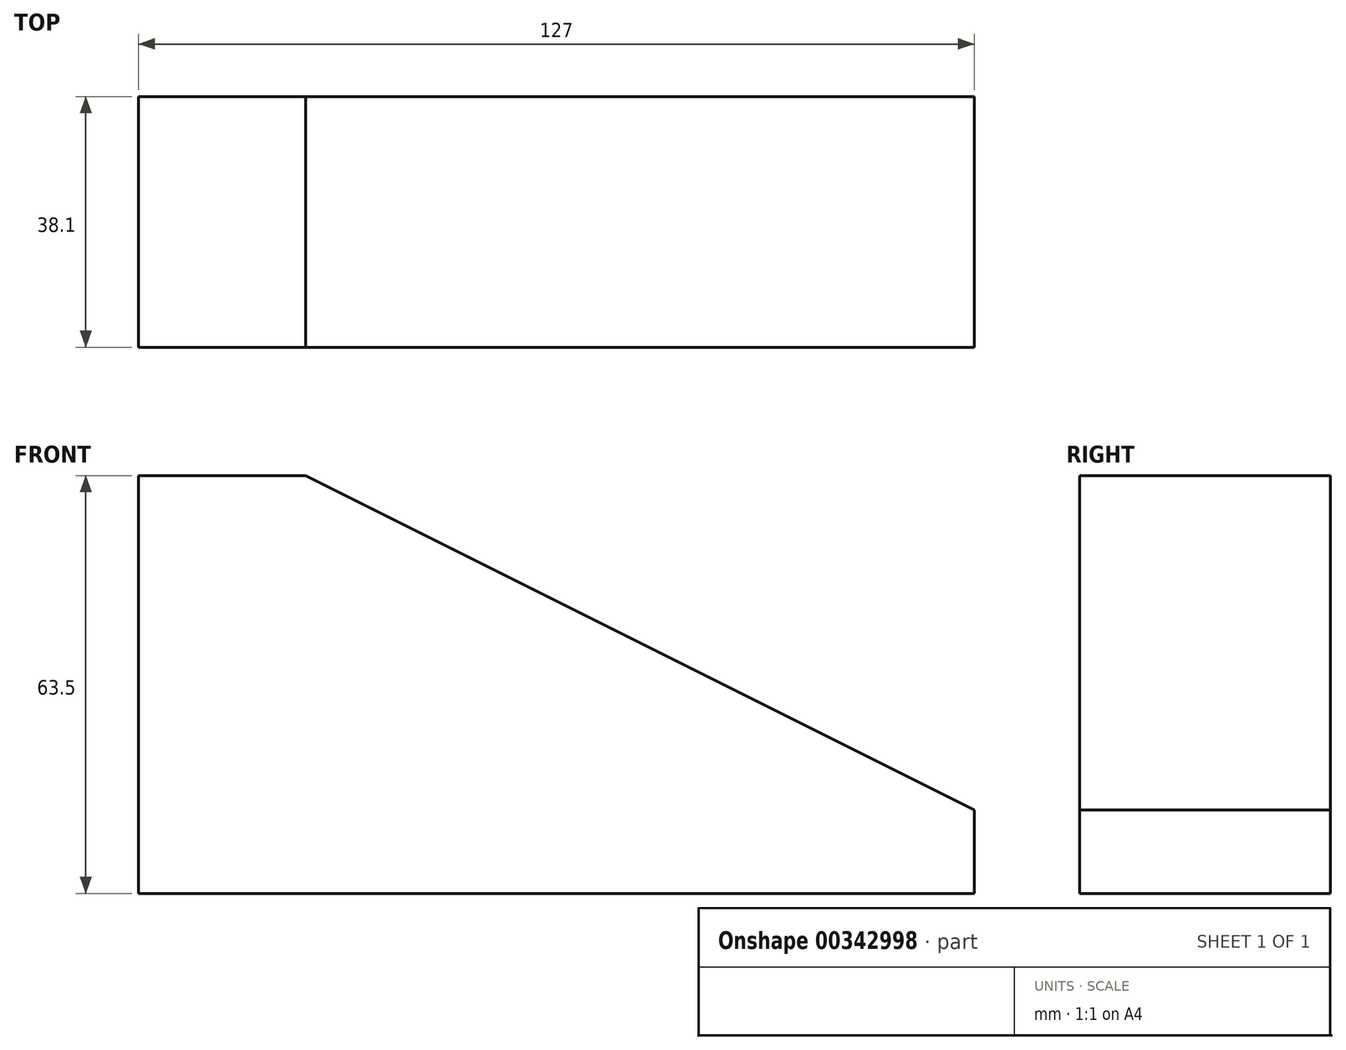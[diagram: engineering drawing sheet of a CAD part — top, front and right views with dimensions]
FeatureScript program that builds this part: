
annotation { "Feature Type Name" : "Feature", "Feature Type Description" : "" }
export const myFeature = defineFeature(function(context is Context, id is Id, definition is map)
    precondition{}
    {
        {
            var Q0;
            Q0=qCreatedBy(makeId("Front.planeOp"),FACE);
            var sketch = newSketch(context, id + "F0", { "sketchPlane" : qUnion([Q0])});
            skLineSegment(sketch, "E0", {"start": v(71.02, -27.23) * mm, "end": v(-55.98, -27.23) * mm});
            skLineSegment(sketch, "E1", {"start": v(-55.98, -27.23) * mm, "end": v(-55.98, 36.27) * mm});
            skLineSegment(sketch, "E2", {"start": v(71.02, -27.23) * mm, "end": v(71.02, -14.53) * mm});
            skLineSegment(sketch, "E3", {"start": v(-55.98, 36.27) * mm, "end": v(-30.58, 36.27) * mm});
            skLineSegment(sketch, "E4", {"start": v(-30.58, 36.27) * mm, "end": v(71.02, -14.53) * mm});
            skSolve(sketch);
        }
        {
            var Q0;
            Q0 = qSketchRegion(id + "F0", true);
            extrude(context, id + "F1", {"entities" : qUnion([Q0]), "depth" : 38.1 * mm});
        }
    });
